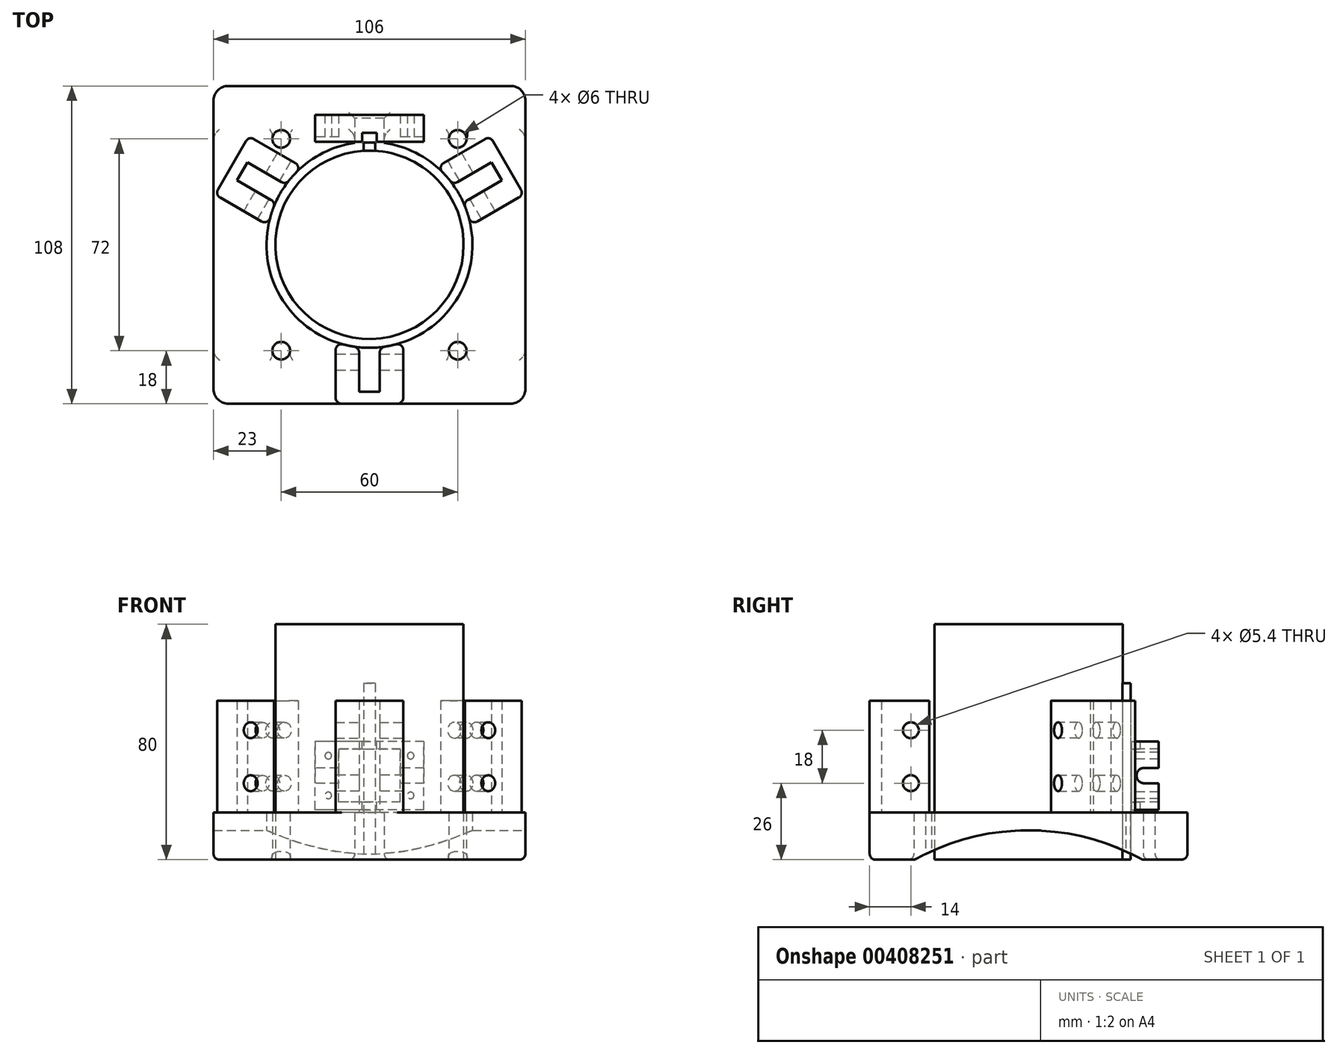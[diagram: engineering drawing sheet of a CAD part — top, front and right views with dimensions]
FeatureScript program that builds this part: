
annotation { "Feature Type Name" : "Feature", "Feature Type Description" : "" }
export const myFeature = defineFeature(function(context is Context, id is Id, definition is map)
    precondition{}
    {
        {
            var Q0;
            Q0=qCreatedBy(makeId("Top.planeOp"),FACE);
            var sketch = newSketch(context, id + "F0", { "sketchPlane" : qUnion([Q0])});
            skLineSegment(sketch, "E0.bottom", {"start": v(48, -54) * mm, "end": v(-48, -54) * mm});
            skLineSegment(sketch, "E0.top", {"start": v(48, 54) * mm, "end": v(-48, 54) * mm});
            skLineSegment(sketch, "E0.left", {"start": v(53, -49) * mm, "end": v(53, 49) * mm});
            skLineSegment(sketch, "E0.right", {"start": v(-53, -49) * mm, "end": v(-53, 49) * mm});
            skPoint(sketch, "E0.middle", {"position": v(0, 0) * mm});
            skArc(sketch, "E1", {"start": v(-5, 34.64) * mm, "mid": v(0, -35) * mm, "end": v(5, 34.64) * mm});
            skCircle(sketch, "E2", {"center": v(-30, 36) * mm, "radius": 3 * mm});
            skCircle(sketch, "E3.MirrorC", {"center": v(30, 36) * mm, "radius": 3 * mm});
            skCircle(sketch, "E4.MirrorC", {"center": v(-30, -36) * mm, "radius": 3 * mm});
            skCircle(sketch, "E5.MirrorC", {"center": v(30, -36) * mm, "radius": 3 * mm});
            skPoint(sketch, "E6.visualSharp", {"position": v(-53, -54) * mm});
            skArc(sketch, "E6.filletArc", {"start": v(-53, -49) * mm, "mid": v(-51.54, -52.54) * mm, "end": v(-48, -54) * mm});
            skPoint(sketch, "E7.visualSharp", {"position": v(53, -54) * mm});
            skArc(sketch, "E7.filletArc", {"start": v(48, -54) * mm, "mid": v(51.54, -52.54) * mm, "end": v(53, -49) * mm});
            skPoint(sketch, "E8.visualSharp", {"position": v(53, 54) * mm});
            skArc(sketch, "E8.filletArc", {"start": v(53, 49) * mm, "mid": v(51.54, 52.54) * mm, "end": v(48, 54) * mm});
            skPoint(sketch, "E9.visualSharp", {"position": v(-53, 54) * mm});
            skArc(sketch, "E9.filletArc", {"start": v(-48, 54) * mm, "mid": v(-51.54, 52.54) * mm, "end": v(-53, 49) * mm});
            skLineSegment(sketch, "E10", {"start": v(0, 0) * mm, "end": v(0, 76.48) * mm, "construction": true});
            skLineSegment(sketch, "E11", {"start": v(5, 34.64) * mm, "end": v(5, 43) * mm});
            skLineSegment(sketch, "E12", {"start": v(5, 43) * mm, "end": v(-5, 43) * mm});
            skLineSegment(sketch, "E13", {"start": v(-5, 43) * mm, "end": v(-5, 34.64) * mm});
            skSolve(sketch);
        }
        {
            var Q0;
            Q0=makeQuery(id+"F0.imprint","IMPRINT",FACE,{"disambiguationData":[TD([[makeQuery(id+"F0.imprint","IMPRINT",EDGE,{"derivedFrom":sQuery(id+"F0.wireOp",EDGE,"E0.bottom")}),-1.0]])]});
            extrude(context, id + "F1", {"entities" : qUnion([Q0]), "depth" : 16 * mm});
        }
        {
            var Q0;
            Q0=qCreatedBy(makeId("Right.planeOp"),FACE);
            cPlane(context, id + "F2", {"entities" : qUnion([Q0]), "cplaneType" : CPlaneType.OFFSET, "offset" : 150 * mm, "width" : 150 * mm, "height" : 150 * mm});
        }
        {
            var Q0;
            Q0=qCreatedBy(id+"F2.planeOp",FACE);
            var sketch = newSketch(context, id + "F3", { "sketchPlane" : qUnion([Q0])});
            skLineSegment(sketch, "E14", {"start": v(0, 0) * mm, "end": v(0, -70) * mm, "construction": true});
            skPoint(sketch, "E14.endSnap0", {"position": v(0, 0) * mm});
            skCircle(sketch, "E15", {"center": v(0, -70) * mm, "radius": 80 * mm});
            skSolve(sketch);
        }
        {
            var Q0;
            Q0 = qSketchRegion(id + "F3", true);
            extrude(context, id + "F4", {"entities" : qUnion([Q0]), "operationType" : NewBodyOperationType.REMOVE, "oppositeDirection" : true, "depth" : 500 * mm});
        }
        {
            var Q0;
            {var subQ0=sQuery(id+"F0.wireOp",EDGE,"E13");var subQ1=sQuery(id+"F0.wireOp",EDGE,"E8.filletArc");var subQ2=sQuery(id+"F0.wireOp",EDGE,"E3.MirrorC");var subQ3=sQuery(id+"F0.wireOp",EDGE,"E9.filletArc");var subQ4=sQuery(id+"F0.wireOp",EDGE,"E0.top");var subQ5=sQuery(id+"F0.wireOp",EDGE,"E11");var subQ6=sQuery(id+"F0.wireOp",EDGE,"E0.left");var subQ7=sQuery(id+"F0.wireOp",EDGE,"E12");var subQ8=sQuery(id+"F0.wireOp",EDGE,"E0.right");var subQ9=sQuery(id+"F0.wireOp",EDGE,"E2");Q0=makeQuery(id+"F4.boolean.opBoolean","SPLIT",FACE,{"disambiguationData":[TD([makeQuery(id+"F1.opExtrude","SWEPT_FACE",FACE,{"disambiguationData":[OSD([subQ4])]})])],"derivedFrom":makeQuery(id+"F1.opExtrude","CAP_FACE",FACE,{"disambiguationData":[OSD([sQuery(id+"F0.wireOp",EDGE,"E0.bottom"),subQ4,subQ6,subQ8,sQuery(id+"F0.wireOp",EDGE,"E1"),subQ9,subQ2,sQuery(id+"F0.wireOp",EDGE,"E4.MirrorC"),sQuery(id+"F0.wireOp",EDGE,"E5.MirrorC"),sQuery(id+"F0.wireOp",EDGE,"E6.filletArc"),sQuery(id+"F0.wireOp",EDGE,"E7.filletArc"),subQ1,subQ3,subQ5,subQ7,subQ0])],"isStart":true})});}
            var Q1;
            {var subQ0=sQuery(id+"F0.wireOp",EDGE,"E4.MirrorC");var subQ1=sQuery(id+"F0.wireOp",EDGE,"E0.left");var subQ2=sQuery(id+"F0.wireOp",EDGE,"E0.right");var subQ3=sQuery(id+"F0.wireOp",EDGE,"E0.bottom");var subQ4=sQuery(id+"F0.wireOp",EDGE,"E6.filletArc");var subQ5=sQuery(id+"F0.wireOp",EDGE,"E5.MirrorC");var subQ6=sQuery(id+"F0.wireOp",EDGE,"E7.filletArc");Q1=makeQuery(id+"F4.boolean.opBoolean","SPLIT",FACE,{"disambiguationData":[TD([makeQuery(id+"F1.opExtrude","SWEPT_FACE",FACE,{"disambiguationData":[OSD([subQ3])]})])],"derivedFrom":makeQuery(id+"F1.opExtrude","CAP_FACE",FACE,{"disambiguationData":[OSD([subQ3,sQuery(id+"F0.wireOp",EDGE,"E0.top"),subQ1,subQ2,sQuery(id+"F0.wireOp",EDGE,"E1"),sQuery(id+"F0.wireOp",EDGE,"E2"),sQuery(id+"F0.wireOp",EDGE,"E3.MirrorC"),subQ0,subQ5,subQ4,subQ6,sQuery(id+"F0.wireOp",EDGE,"E8.filletArc"),sQuery(id+"F0.wireOp",EDGE,"E9.filletArc"),sQuery(id+"F0.wireOp",EDGE,"E11"),sQuery(id+"F0.wireOp",EDGE,"E12"),sQuery(id+"F0.wireOp",EDGE,"E13")])],"isStart":true})});}
            fillet(context, id + "F5", {"entities" : qUnion([Q0, Q1]), "radius" : 2 * mm, "tangentPropagation" : true, "allowEdgeOverflow" : false});
        }
        {
            var Q0;
            Q0=qCreatedBy(makeId("Top.planeOp"),FACE);
            var sketch = newSketch(context, id + "F6", { "sketchPlane" : qUnion([Q0])});
            skCircle(sketch, "E16", {"center": v(0, 0) * mm, "radius": 32 * mm});
            skLineSegment(sketch, "E17", {"start": v(0, 0) * mm, "end": v(0, 34.7) * mm, "construction": true});
            skLineSegment(sketch, "E18", {"start": v(0, 34.7) * mm, "end": v(-2, 34.7) * mm});
            skLineSegment(sketch, "E19", {"start": v(-2, 34.7) * mm, "end": v(-2, 31.94) * mm});
            skLineSegment(sketch, "E20", {"start": v(0, 34.7) * mm, "end": v(2, 34.7) * mm});
            skLineSegment(sketch, "E21", {"start": v(2, 34.7) * mm, "end": v(2, 31.94) * mm});
            skSolve(sketch);
        }
        {
            var Q0;
            Q0=makeQuery(id+"F6.imprint","IMPRINT",FACE,{"disambiguationData":[TD([[makeQuery(id+"F6.imprint","IMPRINT",EDGE,{"derivedFrom":sQuery(id+"F6.wireOp",EDGE,"E16")}),1.0]])]});
            extrude(context, id + "F7", {"entities" : qUnion([Q0]), "depth" : 80 * mm});
        }
        {
            var Q0;
            Q0=makeQuery(id+"F1.opExtrude","CAP_FACE",FACE,{"disambiguationData":[OSD([sQuery(id+"F0.wireOp",EDGE,"E0.bottom"),sQuery(id+"F0.wireOp",EDGE,"E0.top"),sQuery(id+"F0.wireOp",EDGE,"E0.left"),sQuery(id+"F0.wireOp",EDGE,"E0.right"),sQuery(id+"F0.wireOp",EDGE,"E1"),sQuery(id+"F0.wireOp",EDGE,"E2"),sQuery(id+"F0.wireOp",EDGE,"E3.MirrorC"),sQuery(id+"F0.wireOp",EDGE,"E4.MirrorC"),sQuery(id+"F0.wireOp",EDGE,"E5.MirrorC"),sQuery(id+"F0.wireOp",EDGE,"E6.filletArc"),sQuery(id+"F0.wireOp",EDGE,"E7.filletArc"),sQuery(id+"F0.wireOp",EDGE,"E8.filletArc"),sQuery(id+"F0.wireOp",EDGE,"E9.filletArc"),sQuery(id+"F0.wireOp",EDGE,"E11"),sQuery(id+"F0.wireOp",EDGE,"E12"),sQuery(id+"F0.wireOp",EDGE,"E13")])],"isStart":false});
            cPlane(context, id + "F8", {"entities" : qUnion([Q0]), "cplaneType" : CPlaneType.OFFSET, "offset" : 10 * mm, "width" : 150 * mm, "height" : 150 * mm});
        }
        {
            var Q0;
            Q0=qCreatedBy(id+"F8.planeOp",FACE);
            var sketch = newSketch(context, id + "F9", { "sketchPlane" : qUnion([Q0])});
            skCircle(sketch, "E22.0.0", {"center": v(0, 0) * mm, "radius": 32 * mm, "construction": true});
            skLineSegment(sketch, "E23", {"start": v(0, 0) * mm, "end": v(0, -32) * mm, "construction": true});
            skLineSegment(sketch, "E24", {"start": v(0, -32) * mm, "end": v(-2.5, -32) * mm});
            skLineSegment(sketch, "E25", {"start": v(-2.5, -32) * mm, "end": v(-2.5, -37.3) * mm});
            skLineSegment(sketch, "E26", {"start": v(-2.5, -37.3) * mm, "end": v(-12.5, -37.3) * mm});
            skLineSegment(sketch, "E27", {"start": v(-12.5, -37.3) * mm, "end": v(-12.5, -40) * mm});
            skLineSegment(sketch, "E28", {"start": v(-12.5, -40) * mm, "end": v(12.5, -40) * mm});
            skLineSegment(sketch, "E29", {"start": v(12.5, -40) * mm, "end": v(12.5, -37.3) * mm});
            skLineSegment(sketch, "E30", {"start": v(0, -32) * mm, "end": v(2.5, -32) * mm});
            skLineSegment(sketch, "E31", {"start": v(2.5, -32) * mm, "end": v(2.5, -37.3) * mm});
            skLineSegment(sketch, "E32", {"start": v(2.5, -37.3) * mm, "end": v(12.5, -37.3) * mm});
            skSolve(sketch);
        }
        {
            var Q0;
            Q0=qCreatedBy(id+"F8.planeOp",FACE);
            cPlane(context, id + "F10", {"entities" : qUnion([Q0]), "cplaneType" : CPlaneType.OFFSET, "offset" : 18 * mm, "width" : 150 * mm, "height" : 150 * mm});
        }
        {
            var Q0;
            Q0=qCreatedBy(id+"F10.planeOp",FACE);
            var sketch = newSketch(context, id + "F11", { "sketchPlane" : qUnion([Q0])});
            skPoint(sketch, "E33.center", {"position": v(-0.32, 7.69) * mm});
            skCircle(sketch, "E34.0", {"center": v(0, 0) * mm, "radius": 32 * mm, "construction": true});
            skLineSegment(sketch, "E35", {"start": v(0, 0) * mm, "end": v(0, -32) * mm, "construction": true});
            skLineSegment(sketch, "E36", {"start": v(0, -32) * mm, "end": v(2.5, -32) * mm});
            skLineSegment(sketch, "E37", {"start": v(2.5, -32) * mm, "end": v(2.5, -37.3) * mm});
            skLineSegment(sketch, "E38", {"start": v(2.5, -37.3) * mm, "end": v(12.5, -37.3) * mm});
            skLineSegment(sketch, "E39", {"start": v(12.5, -37.3) * mm, "end": v(12.5, -40) * mm});
            skLineSegment(sketch, "E40", {"start": v(12.5, -40) * mm, "end": v(-12.5, -40) * mm});
            skLineSegment(sketch, "E41", {"start": v(-12.5, -40) * mm, "end": v(-12.5, -37.3) * mm});
            skLineSegment(sketch, "E42", {"start": v(-12.5, -37.3) * mm, "end": v(-2.5, -37.3) * mm});
            skLineSegment(sketch, "E43", {"start": v(-2.5, -37.3) * mm, "end": v(-2.5, -32) * mm});
            skLineSegment(sketch, "E44", {"start": v(-2.5, -32) * mm, "end": v(0, -32) * mm});
            skSolve(sketch);
        }
        {
            var Q0;
            Q0 = qSketchRegion(id + "F11", true);
            var Q1;
            Q1=sQuery(id+"F11.wireOp",EDGE,"E40");
            revolve(context, id + "F12", {"entities" : qUnion([Q0]), "axis" : qUnion([Q1]), "revolveType" : RevolveType.FULL});
        }
        {
            var Q0;
            Q0=makeQuery(id+"F9.imprint","IMPRINT",FACE,{"disambiguationData":[TD([[makeQuery(id+"F9.imprint","IMPRINT",EDGE,{"derivedFrom":sQuery(id+"F9.wireOp",EDGE,"E24")}),1.0]])]});
            var Q1;
            Q1=sQuery(id+"F9.wireOp",EDGE,"E28");
            revolve(context, id + "F13", {"entities" : qUnion([Q0]), "axis" : qUnion([Q1]), "revolveType" : RevolveType.FULL});
        }
        {
            var Q0;
            Q0=makeQuery(id+"F13.opRevolve","SWEPT_BODY",BODY,{"disambiguationData":[OSD([sQuery(id+"F9.wireOp",EDGE,"E24"),sQuery(id+"F9.wireOp",EDGE,"E25"),sQuery(id+"F9.wireOp",EDGE,"E26"),sQuery(id+"F9.wireOp",EDGE,"E27"),sQuery(id+"F9.wireOp",EDGE,"E28"),sQuery(id+"F9.wireOp",EDGE,"E29"),sQuery(id+"F9.wireOp",EDGE,"E30"),sQuery(id+"F9.wireOp",EDGE,"E31"),sQuery(id+"F9.wireOp",EDGE,"E32")])]});
            var Q1;
            Q1=makeQuery(id+"F12.opRevolve","SWEPT_BODY",BODY,{"disambiguationData":[OSD([sQuery(id+"F11.wireOp",EDGE,"E36"),sQuery(id+"F11.wireOp",EDGE,"E37"),sQuery(id+"F11.wireOp",EDGE,"E38"),sQuery(id+"F11.wireOp",EDGE,"E39"),sQuery(id+"F11.wireOp",EDGE,"E40"),sQuery(id+"F11.wireOp",EDGE,"E41"),sQuery(id+"F11.wireOp",EDGE,"E42"),sQuery(id+"F11.wireOp",EDGE,"E43"),sQuery(id+"F11.wireOp",EDGE,"E44")])]});
            var Q2;
            Q2=makeQuery(id+"F7.opExtrude","SWEPT_FACE",FACE,{"disambiguationData":[OSD([sQuery(id+"F6.wireOp",EDGE,"E16")])]});
            circularPattern(context, id + "F14", {"entities" : qUnion([Q0, Q1]), "axis" : qUnion([Q2]), "angle" : 360 * degree, "instanceCount" : 3, "equalSpace" : true});
        }
        {
            var Q0;
            Q0=makeQuery(id+"F1.opExtrude","CAP_FACE",FACE,{"disambiguationData":[OSD([sQuery(id+"F0.wireOp",EDGE,"E0.bottom"),sQuery(id+"F0.wireOp",EDGE,"E0.top"),sQuery(id+"F0.wireOp",EDGE,"E0.left"),sQuery(id+"F0.wireOp",EDGE,"E0.right"),sQuery(id+"F0.wireOp",EDGE,"E1"),sQuery(id+"F0.wireOp",EDGE,"E2"),sQuery(id+"F0.wireOp",EDGE,"E3.MirrorC"),sQuery(id+"F0.wireOp",EDGE,"E4.MirrorC"),sQuery(id+"F0.wireOp",EDGE,"E5.MirrorC"),sQuery(id+"F0.wireOp",EDGE,"E6.filletArc"),sQuery(id+"F0.wireOp",EDGE,"E7.filletArc"),sQuery(id+"F0.wireOp",EDGE,"E8.filletArc"),sQuery(id+"F0.wireOp",EDGE,"E9.filletArc"),sQuery(id+"F0.wireOp",EDGE,"E11"),sQuery(id+"F0.wireOp",EDGE,"E12"),sQuery(id+"F0.wireOp",EDGE,"E13")])],"isStart":false});
            var sketch = newSketch(context, id + "F15", { "sketchPlane" : qUnion([Q0])});
            skLineSegment(sketch, "E45", {"start": v(0, -54) * mm, "end": v(0, -49.97) * mm});
            skLineSegment(sketch, "E46", {"start": v(-11.5, -54) * mm, "end": v(-11.5, -33.06) * mm});
            skLineSegment(sketch, "E47", {"start": v(0, -49.97) * mm, "end": v(-3.5, -49.97) * mm});
            skLineSegment(sketch, "E48", {"start": v(-3.5, -49.97) * mm, "end": v(-3.5, -34.82) * mm});
            skLineSegment(sketch, "E49.MirrorCS", {"start": v(0, -49.97) * mm, "end": v(3.5, -49.97) * mm});
            skLineSegment(sketch, "E50.MirrorCS", {"start": v(3.5, -49.97) * mm, "end": v(3.5, -34.82) * mm});
            skLineSegment(sketch, "E51.MirrorCS", {"start": v(11.5, -54) * mm, "end": v(11.5, -33.06) * mm});
            skSolve(sketch);
        }
        {
            var Q0;
            {var subQ2=sQuery(id+"F15.wireOp",EDGE,"E45");Q0=makeQuery(id+"F15.imprint","IMPRINT",FACE,{"disambiguationData":[TD([[makeQuery(id+"F15.imprint","IMPRINT",EDGE,{"derivedFrom":subQ2}),1.0]])]});}
            var Q1;
            {var subQ2=sQuery(id+"F15.wireOp",EDGE,"E45");Q1=makeQuery(id+"F15.imprint","IMPRINT",FACE,{"disambiguationData":[TD([[makeQuery(id+"F15.imprint","IMPRINT",EDGE,{"derivedFrom":subQ2}),-1.0]])]});}
            extrude(context, id + "F16", {"entities" : qUnion([Q0, Q1]), "depth" : (2 + 2 + 16 + 16 + 2) * mm});
        }
        {
            var Q0;
            Q0=makeQuery(id+"F16.opExtrude","SWEPT_BODY",BODY,{"disambiguationData":[OSD([sQuery(id+"F0.wireOp",EDGE,"E0.bottom"),sQuery(id+"F0.wireOp",EDGE,"E1"),sQuery(id+"F15.wireOp",EDGE,"E46"),sQuery(id+"F15.wireOp",EDGE,"E47"),sQuery(id+"F15.wireOp",EDGE,"E48"),sQuery(id+"F15.wireOp",EDGE,"E49.MirrorCS"),sQuery(id+"F15.wireOp",EDGE,"E50.MirrorCS"),sQuery(id+"F15.wireOp",EDGE,"E51.MirrorCS")])]});
            var Q1;
            Q1=makeQuery(id+"F7.opExtrude","SWEPT_FACE",FACE,{"disambiguationData":[OSD([sQuery(id+"F6.wireOp",EDGE,"E16")])]});
            circularPattern(context, id + "F17", {"entities" : qUnion([Q0]), "axis" : qUnion([Q1]), "angle" : 360 * degree, "instanceCount" : 3, "equalSpace" : true});
        }
        {
            var Q0;
            Q0=makeQuery(id+"F17.opPattern","COPY",EDGE,{"derivedFrom":makeQuery(id+"F16.opExtrude","SWEPT_EDGE",EDGE,{"disambiguationData":[OSD([sQuery(id+"F0.wireOp",EDGE,"E0.bottom"),sQuery(id+"F15.wireOp",EDGE,"E46")])]}),"instanceName":"2"});
            var Q1;
            Q1=makeQuery(id+"F17.opPattern","COPY",EDGE,{"derivedFrom":makeQuery(id+"F16.opExtrude","SWEPT_EDGE",EDGE,{"disambiguationData":[OSD([sQuery(id+"F0.wireOp",EDGE,"E0.bottom"),sQuery(id+"F15.wireOp",EDGE,"E51.MirrorCS")])]}),"instanceName":"2"});
            var Q2;
            Q2=makeQuery(id+"F17.opPattern","COPY",EDGE,{"derivedFrom":makeQuery(id+"F16.opExtrude","SWEPT_EDGE",EDGE,{"disambiguationData":[OSD([sQuery(id+"F0.wireOp",EDGE,"E1"),sQuery(id+"F15.wireOp",EDGE,"E51.MirrorCS")])]}),"instanceName":"2"});
            var Q3;
            Q3=makeQuery(id+"F17.opPattern","COPY",EDGE,{"derivedFrom":makeQuery(id+"F16.opExtrude","SWEPT_EDGE",EDGE,{"disambiguationData":[OSD([sQuery(id+"F0.wireOp",EDGE,"E1"),sQuery(id+"F15.wireOp",EDGE,"E46")])]}),"instanceName":"2"});
            var Q4;
            Q4=makeQuery(id+"F17.opPattern","COPY",EDGE,{"derivedFrom":makeQuery(id+"F16.opExtrude","SWEPT_EDGE",EDGE,{"disambiguationData":[OSD([sQuery(id+"F0.wireOp",EDGE,"E1"),sQuery(id+"F15.wireOp",EDGE,"E46")])]}),"instanceName":"1"});
            var Q5;
            Q5=makeQuery(id+"F17.opPattern","COPY",EDGE,{"derivedFrom":makeQuery(id+"F16.opExtrude","SWEPT_EDGE",EDGE,{"disambiguationData":[OSD([sQuery(id+"F0.wireOp",EDGE,"E0.bottom"),sQuery(id+"F15.wireOp",EDGE,"E46")])]}),"instanceName":"1"});
            var Q6;
            Q6=makeQuery(id+"F17.opPattern","COPY",EDGE,{"derivedFrom":makeQuery(id+"F16.opExtrude","SWEPT_EDGE",EDGE,{"disambiguationData":[OSD([sQuery(id+"F0.wireOp",EDGE,"E0.bottom"),sQuery(id+"F15.wireOp",EDGE,"E51.MirrorCS")])]}),"instanceName":"1"});
            var Q7;
            Q7=makeQuery(id+"F17.opPattern","COPY",EDGE,{"derivedFrom":makeQuery(id+"F16.opExtrude","SWEPT_EDGE",EDGE,{"disambiguationData":[OSD([sQuery(id+"F0.wireOp",EDGE,"E1"),sQuery(id+"F15.wireOp",EDGE,"E51.MirrorCS")])]}),"instanceName":"1"});
            var Q8;
            Q8=makeQuery(id+"F16.opExtrude","SWEPT_EDGE",EDGE,{"disambiguationData":[OSD([sQuery(id+"F0.wireOp",EDGE,"E1"),sQuery(id+"F15.wireOp",EDGE,"E51.MirrorCS")])]});
            var Q9;
            Q9=makeQuery(id+"F16.opExtrude","SWEPT_EDGE",EDGE,{"disambiguationData":[OSD([sQuery(id+"F0.wireOp",EDGE,"E0.bottom"),sQuery(id+"F15.wireOp",EDGE,"E51.MirrorCS")])]});
            var Q10;
            Q10=makeQuery(id+"F16.opExtrude","SWEPT_EDGE",EDGE,{"disambiguationData":[OSD([sQuery(id+"F0.wireOp",EDGE,"E0.bottom"),sQuery(id+"F15.wireOp",EDGE,"E46")])]});
            var Q11;
            Q11=makeQuery(id+"F16.opExtrude","SWEPT_EDGE",EDGE,{"disambiguationData":[OSD([sQuery(id+"F0.wireOp",EDGE,"E1"),sQuery(id+"F15.wireOp",EDGE,"E46")])]});
            fillet(context, id + "F18", {"entities" : qUnion([Q0, Q1, Q2, Q3, Q4, Q5, Q6, Q7, Q8, Q9, Q10, Q11]), "radius" : 2 * mm, "tangentPropagation" : true, "allowEdgeOverflow" : false});
        }
        {
            var Q0;
            Q0=makeQuery(id+"F17.opPattern","COPY",EDGE,{"derivedFrom":makeQuery(id+"F16.opExtrude","SWEPT_EDGE",EDGE,{"disambiguationData":[OSD([sQuery(id+"F0.wireOp",EDGE,"E1"),sQuery(id+"F15.wireOp",EDGE,"E48")])]}),"instanceName":"1"});
            var Q1;
            Q1=makeQuery(id+"F17.opPattern","COPY",EDGE,{"derivedFrom":makeQuery(id+"F16.opExtrude","SWEPT_EDGE",EDGE,{"disambiguationData":[OSD([sQuery(id+"F0.wireOp",EDGE,"E1"),sQuery(id+"F15.wireOp",EDGE,"E50.MirrorCS")])]}),"instanceName":"1"});
            var Q2;
            Q2=makeQuery(id+"F17.opPattern","COPY",EDGE,{"derivedFrom":makeQuery(id+"F16.opExtrude","SWEPT_EDGE",EDGE,{"disambiguationData":[OSD([sQuery(id+"F0.wireOp",EDGE,"E1"),sQuery(id+"F15.wireOp",EDGE,"E48")])]}),"instanceName":"2"});
            var Q3;
            Q3=makeQuery(id+"F17.opPattern","COPY",EDGE,{"derivedFrom":makeQuery(id+"F16.opExtrude","SWEPT_EDGE",EDGE,{"disambiguationData":[OSD([sQuery(id+"F0.wireOp",EDGE,"E1"),sQuery(id+"F15.wireOp",EDGE,"E50.MirrorCS")])]}),"instanceName":"2"});
            var Q4;
            Q4=makeQuery(id+"F16.opExtrude","SWEPT_EDGE",EDGE,{"disambiguationData":[OSD([sQuery(id+"F0.wireOp",EDGE,"E1"),sQuery(id+"F15.wireOp",EDGE,"E50.MirrorCS")])]});
            var Q5;
            Q5=makeQuery(id+"F16.opExtrude","SWEPT_EDGE",EDGE,{"disambiguationData":[OSD([sQuery(id+"F0.wireOp",EDGE,"E1"),sQuery(id+"F15.wireOp",EDGE,"E48")])]});
            fillet(context, id + "F19", {"entities" : qUnion([Q0, Q1, Q2, Q3, Q4, Q5]), "radius" : 2 * mm, "tangentPropagation" : true, "allowEdgeOverflow" : false});
        }
        {
            var Q0;
            Q0=makeQuery(id+"F17.opPattern","COPY",BODY,{"derivedFrom":makeQuery(id+"F16.opExtrude","SWEPT_BODY",BODY,{"disambiguationData":[OSD([sQuery(id+"F0.wireOp",EDGE,"E0.bottom"),sQuery(id+"F0.wireOp",EDGE,"E1"),sQuery(id+"F15.wireOp",EDGE,"E46"),sQuery(id+"F15.wireOp",EDGE,"E47"),sQuery(id+"F15.wireOp",EDGE,"E48"),sQuery(id+"F15.wireOp",EDGE,"E49.MirrorCS"),sQuery(id+"F15.wireOp",EDGE,"E50.MirrorCS"),sQuery(id+"F15.wireOp",EDGE,"E51.MirrorCS")])]}),"instanceName":"2"});
            var Q1;
            Q1=makeQuery(id+"F17.opPattern","COPY",BODY,{"derivedFrom":makeQuery(id+"F16.opExtrude","SWEPT_BODY",BODY,{"disambiguationData":[OSD([sQuery(id+"F0.wireOp",EDGE,"E0.bottom"),sQuery(id+"F0.wireOp",EDGE,"E1"),sQuery(id+"F15.wireOp",EDGE,"E46"),sQuery(id+"F15.wireOp",EDGE,"E47"),sQuery(id+"F15.wireOp",EDGE,"E48"),sQuery(id+"F15.wireOp",EDGE,"E49.MirrorCS"),sQuery(id+"F15.wireOp",EDGE,"E50.MirrorCS"),sQuery(id+"F15.wireOp",EDGE,"E51.MirrorCS")])]}),"instanceName":"1"});
            var Q2;
            Q2=makeQuery(id+"F16.opExtrude","SWEPT_BODY",BODY,{"disambiguationData":[OSD([sQuery(id+"F0.wireOp",EDGE,"E0.bottom"),sQuery(id+"F0.wireOp",EDGE,"E1"),sQuery(id+"F15.wireOp",EDGE,"E46"),sQuery(id+"F15.wireOp",EDGE,"E47"),sQuery(id+"F15.wireOp",EDGE,"E48"),sQuery(id+"F15.wireOp",EDGE,"E49.MirrorCS"),sQuery(id+"F15.wireOp",EDGE,"E50.MirrorCS"),sQuery(id+"F15.wireOp",EDGE,"E51.MirrorCS")])]});
            var Q3;
            Q3=makeQuery(id+"F1.opExtrude","SWEPT_BODY",BODY,{"disambiguationData":[OSD([sQuery(id+"F0.wireOp",EDGE,"E0.bottom"),sQuery(id+"F0.wireOp",EDGE,"E0.top"),sQuery(id+"F0.wireOp",EDGE,"E0.left"),sQuery(id+"F0.wireOp",EDGE,"E0.right"),sQuery(id+"F0.wireOp",EDGE,"E1"),sQuery(id+"F0.wireOp",EDGE,"E2"),sQuery(id+"F0.wireOp",EDGE,"E3.MirrorC"),sQuery(id+"F0.wireOp",EDGE,"E4.MirrorC"),sQuery(id+"F0.wireOp",EDGE,"E5.MirrorC"),sQuery(id+"F0.wireOp",EDGE,"E6.filletArc"),sQuery(id+"F0.wireOp",EDGE,"E7.filletArc"),sQuery(id+"F0.wireOp",EDGE,"E8.filletArc"),sQuery(id+"F0.wireOp",EDGE,"E9.filletArc"),sQuery(id+"F0.wireOp",EDGE,"E11"),sQuery(id+"F0.wireOp",EDGE,"E12"),sQuery(id+"F0.wireOp",EDGE,"E13")])]});
            booleanBodies(context, id + "F20", {"operationType" : BooleanOperationType.UNION, "tools" : qUnion([Q0, Q1, Q2, Q3])});
        }
        {
            var Q0;
            Q0=makeQuery(id+"F14.opPattern","COPY",BODY,{"derivedFrom":makeQuery(id+"F13.opRevolve","SWEPT_BODY",BODY,{"disambiguationData":[OSD([sQuery(id+"F9.wireOp",EDGE,"E24"),sQuery(id+"F9.wireOp",EDGE,"E25"),sQuery(id+"F9.wireOp",EDGE,"E26"),sQuery(id+"F9.wireOp",EDGE,"E27"),sQuery(id+"F9.wireOp",EDGE,"E28"),sQuery(id+"F9.wireOp",EDGE,"E29"),sQuery(id+"F9.wireOp",EDGE,"E30"),sQuery(id+"F9.wireOp",EDGE,"E31"),sQuery(id+"F9.wireOp",EDGE,"E32")])]}),"instanceName":"2"});
            var Q1;
            Q1=makeQuery(id+"F14.opPattern","COPY",BODY,{"derivedFrom":makeQuery(id+"F13.opRevolve","SWEPT_BODY",BODY,{"disambiguationData":[OSD([sQuery(id+"F9.wireOp",EDGE,"E24"),sQuery(id+"F9.wireOp",EDGE,"E25"),sQuery(id+"F9.wireOp",EDGE,"E26"),sQuery(id+"F9.wireOp",EDGE,"E27"),sQuery(id+"F9.wireOp",EDGE,"E28"),sQuery(id+"F9.wireOp",EDGE,"E29"),sQuery(id+"F9.wireOp",EDGE,"E30"),sQuery(id+"F9.wireOp",EDGE,"E31"),sQuery(id+"F9.wireOp",EDGE,"E32")])]}),"instanceName":"1"});
            var Q2;
            Q2=makeQuery(id+"F13.opRevolve","SWEPT_BODY",BODY,{"disambiguationData":[OSD([sQuery(id+"F9.wireOp",EDGE,"E24"),sQuery(id+"F9.wireOp",EDGE,"E25"),sQuery(id+"F9.wireOp",EDGE,"E26"),sQuery(id+"F9.wireOp",EDGE,"E27"),sQuery(id+"F9.wireOp",EDGE,"E28"),sQuery(id+"F9.wireOp",EDGE,"E29"),sQuery(id+"F9.wireOp",EDGE,"E30"),sQuery(id+"F9.wireOp",EDGE,"E31"),sQuery(id+"F9.wireOp",EDGE,"E32")])]});
            var Q3;
            Q3=makeQuery(id+"F12.opRevolve","SWEPT_BODY",BODY,{"disambiguationData":[OSD([sQuery(id+"F11.wireOp",EDGE,"E36"),sQuery(id+"F11.wireOp",EDGE,"E37"),sQuery(id+"F11.wireOp",EDGE,"E38"),sQuery(id+"F11.wireOp",EDGE,"E39"),sQuery(id+"F11.wireOp",EDGE,"E40"),sQuery(id+"F11.wireOp",EDGE,"E41"),sQuery(id+"F11.wireOp",EDGE,"E42"),sQuery(id+"F11.wireOp",EDGE,"E43"),sQuery(id+"F11.wireOp",EDGE,"E44")])]});
            var Q4;
            Q4=makeQuery(id+"F14.opPattern","COPY",BODY,{"derivedFrom":makeQuery(id+"F12.opRevolve","SWEPT_BODY",BODY,{"disambiguationData":[OSD([sQuery(id+"F11.wireOp",EDGE,"E36"),sQuery(id+"F11.wireOp",EDGE,"E37"),sQuery(id+"F11.wireOp",EDGE,"E38"),sQuery(id+"F11.wireOp",EDGE,"E39"),sQuery(id+"F11.wireOp",EDGE,"E40"),sQuery(id+"F11.wireOp",EDGE,"E41"),sQuery(id+"F11.wireOp",EDGE,"E42"),sQuery(id+"F11.wireOp",EDGE,"E43"),sQuery(id+"F11.wireOp",EDGE,"E44")])]}),"instanceName":"1"});
            var Q5;
            Q5=makeQuery(id+"F14.opPattern","COPY",BODY,{"derivedFrom":makeQuery(id+"F12.opRevolve","SWEPT_BODY",BODY,{"disambiguationData":[OSD([sQuery(id+"F11.wireOp",EDGE,"E36"),sQuery(id+"F11.wireOp",EDGE,"E37"),sQuery(id+"F11.wireOp",EDGE,"E38"),sQuery(id+"F11.wireOp",EDGE,"E39"),sQuery(id+"F11.wireOp",EDGE,"E40"),sQuery(id+"F11.wireOp",EDGE,"E41"),sQuery(id+"F11.wireOp",EDGE,"E42"),sQuery(id+"F11.wireOp",EDGE,"E43"),sQuery(id+"F11.wireOp",EDGE,"E44")])]}),"instanceName":"2"});
            var Q6;
            Q6=makeQuery(id+"F17.opPattern","COPY",BODY,{"derivedFrom":makeQuery(id+"F16.opExtrude","SWEPT_BODY",BODY,{"disambiguationData":[OSD([sQuery(id+"F0.wireOp",EDGE,"E0.bottom"),sQuery(id+"F0.wireOp",EDGE,"E1"),sQuery(id+"F15.wireOp",EDGE,"E46"),sQuery(id+"F15.wireOp",EDGE,"E47"),sQuery(id+"F15.wireOp",EDGE,"E48"),sQuery(id+"F15.wireOp",EDGE,"E49.MirrorCS"),sQuery(id+"F15.wireOp",EDGE,"E50.MirrorCS"),sQuery(id+"F15.wireOp",EDGE,"E51.MirrorCS")])]}),"instanceName":"2"});
            booleanBodies(context, id + "F21", {"operationType" : BooleanOperationType.SUBTRACTION, "tools" : qUnion([Q0, Q1, Q2, Q3, Q4, Q5]), "targets" : qUnion([Q6])});
        }
        {
            var Q0;
            Q0 = qSketchRegion(id + "F6", true);
            extrude(context, id + "F22", {"entities" : qUnion([Q0]), "operationType" : NewBodyOperationType.ADD, "depth" : 60 * mm});
        }
        {
            var Q0;
            Q0=qCreatedBy(makeId("Right.planeOp"),FACE);
            var sketch = newSketch(context, id + "F23", { "sketchPlane" : qUnion([Q0])});
            skLineSegment(sketch, "E52", {"start": v(35.08, 40.2) * mm, "end": v(44.2, 40.2) * mm});
            skLineSegment(sketch, "E53", {"start": v(44.2, 40.2) * mm, "end": v(44.2, 31.2) * mm});
            skLineSegment(sketch, "E54", {"start": v(44.2, 31.2) * mm, "end": v(39.3, 31.2) * mm});
            skArc(sketch, "E55", {"start": v(39.3, 31.2) * mm, "mid": v(37.46, 30.44) * mm, "end": v(36.7, 28.6) * mm});
            skLineSegment(sketch, "E56", {"start": v(35.08, 40.2) * mm, "end": v(35.08, 28.6) * mm});
            skLineSegment(sketch, "E57", {"start": v(35.08, 28.6) * mm, "end": v(36.7, 28.6) * mm});
            skLineSegment(sketch, "E58.MirrorCS", {"start": v(35.08, 17) * mm, "end": v(44.2, 17) * mm});
            skLineSegment(sketch, "E59.MirrorCS", {"start": v(35.08, 17) * mm, "end": v(35.08, 28.6) * mm});
            skArc(sketch, "E60.MirrorCS", {"start": v(39.3, 26) * mm, "mid": v(37.46, 26.76) * mm, "end": v(36.7, 28.6) * mm});
            skLineSegment(sketch, "E61.MirrorCS", {"start": v(44.2, 26) * mm, "end": v(39.3, 26) * mm});
            skLineSegment(sketch, "E62.MirrorCS", {"start": v(44.2, 17) * mm, "end": v(44.2, 26) * mm});
            skSolve(sketch);
        }
        {
            var Q0;
            Q0=makeQuery(id+"F23.imprint","IMPRINT",FACE,{"disambiguationData":[TD([[makeQuery(id+"F23.imprint","IMPRINT",EDGE,{"derivedFrom":sQuery(id+"F23.wireOp",EDGE,"E57")}),-1.0]])]});
            var Q1;
            Q1=makeQuery(id+"F23.imprint","IMPRINT",FACE,{"disambiguationData":[TD([[makeQuery(id+"F23.imprint","IMPRINT",EDGE,{"derivedFrom":sQuery(id+"F23.wireOp",EDGE,"E52")}),-1.0]])]});
            extrude(context, id + "F24", {"entities" : qUnion([Q0, Q1]), "operationType" : NewBodyOperationType.ADD, "depth" : 18.5 * mm, "hasSecondDirection" : true, "secondDirectionOppositeDirection" : true, "secondDirectionDepth" : 18.5 * mm});
        }
        {
            var Q0;
            Q0=makeQuery(id+"F24.opExtrude","SWEPT_FACE",FACE,{"disambiguationData":[OSD([sQuery(id+"F23.wireOp",EDGE,"E56"),sQuery(id+"F23.wireOp",EDGE,"E59.MirrorCS")])]});
            var sketch = newSketch(context, id + "F25", { "sketchPlane" : qUnion([Q0])});
            skLineSegment(sketch, "E63.bottom", {"start": v(10.5, 19.6) * mm, "end": v(-10.5, 19.6) * mm});
            skLineSegment(sketch, "E63.top", {"start": v(10.5, 37.6) * mm, "end": v(-10.5, 37.6) * mm});
            skLineSegment(sketch, "E63.left", {"start": v(10.5, 19.6) * mm, "end": v(10.5, 37.6) * mm});
            skLineSegment(sketch, "E63.right", {"start": v(-10.5, 19.6) * mm, "end": v(-10.5, 37.6) * mm});
            skPoint(sketch, "E63.middle", {"position": v(0, 28.6) * mm});
            skLineSegment(sketch, "E64", {"start": v(0, 40.2) * mm, "end": v(0, 17) * mm, "construction": true});
            skLineSegment(sketch, "E65.bottom", {"start": v(14, 35.35) * mm, "end": v(-14, 35.35) * mm, "construction": true});
            skLineSegment(sketch, "E65.top", {"start": v(14, 21.85) * mm, "end": v(-14, 21.85) * mm, "construction": true});
            skLineSegment(sketch, "E65.left", {"start": v(14, 35.35) * mm, "end": v(14, 21.85) * mm, "construction": true});
            skLineSegment(sketch, "E65.right", {"start": v(-14, 35.35) * mm, "end": v(-14, 21.85) * mm, "construction": true});
            skCircle(sketch, "E66", {"center": v(-14, 35.35) * mm, "radius": 1.13 * mm});
            skCircle(sketch, "E67", {"center": v(14, 35.35) * mm, "radius": 1.13 * mm});
            skCircle(sketch, "E68", {"center": v(14, 21.85) * mm, "radius": 1.13 * mm});
            skCircle(sketch, "E69", {"center": v(-14, 21.85) * mm, "radius": 1.13 * mm});
            skSolve(sketch);
        }
        {
            var Q0;
            Q0 = qSketchRegion(id + "F25", true);
            extrude(context, id + "F26", {"entities" : qUnion([Q0]), "operationType" : NewBodyOperationType.REMOVE, "endBound" : BoundingType.THROUGH_ALL, "oppositeDirection" : true, "depth" : 25 * mm});
        }
        {
            var Q0;
            Q0=makeQuery(id+"F24.opExtrude","SWEPT_FACE",FACE,{"disambiguationData":[OSD([sQuery(id+"F23.wireOp",EDGE,"E52")])]});
            var sketch = newSketch(context, id + "F27", { "sketchPlane" : qUnion([Q0])});
            skLineSegment(sketch, "E70", {"start": v(0, 35.08) * mm, "end": v(-2.5, 35.08) * mm});
            skLineSegment(sketch, "E71", {"start": v(-2.5, 35.08) * mm, "end": v(-2.5, 38.08) * mm});
            skLineSegment(sketch, "E72", {"start": v(-2.5, 38.08) * mm, "end": v(2.5, 38.08) * mm});
            skLineSegment(sketch, "E73", {"start": v(2.5, 38.08) * mm, "end": v(2.5, 35.08) * mm});
            skLineSegment(sketch, "E74", {"start": v(2.5, 35.08) * mm, "end": v(0, 35.08) * mm});
            skSolve(sketch);
        }
        {
            var Q0;
            Q0=makeQuery(id+"F27.imprint","IMPRINT",FACE,{"disambiguationData":[TD([[makeQuery(id+"F27.imprint","IMPRINT",EDGE,{"derivedFrom":sQuery(id+"F27.wireOp",EDGE,"E70")}),-1.0]])]});
            extrude(context, id + "F28", {"entities" : qUnion([Q0]), "operationType" : NewBodyOperationType.REMOVE, "endBound" : BoundingType.THROUGH_ALL, "oppositeDirection" : true, "depth" : 25 * mm});
        }
    });
